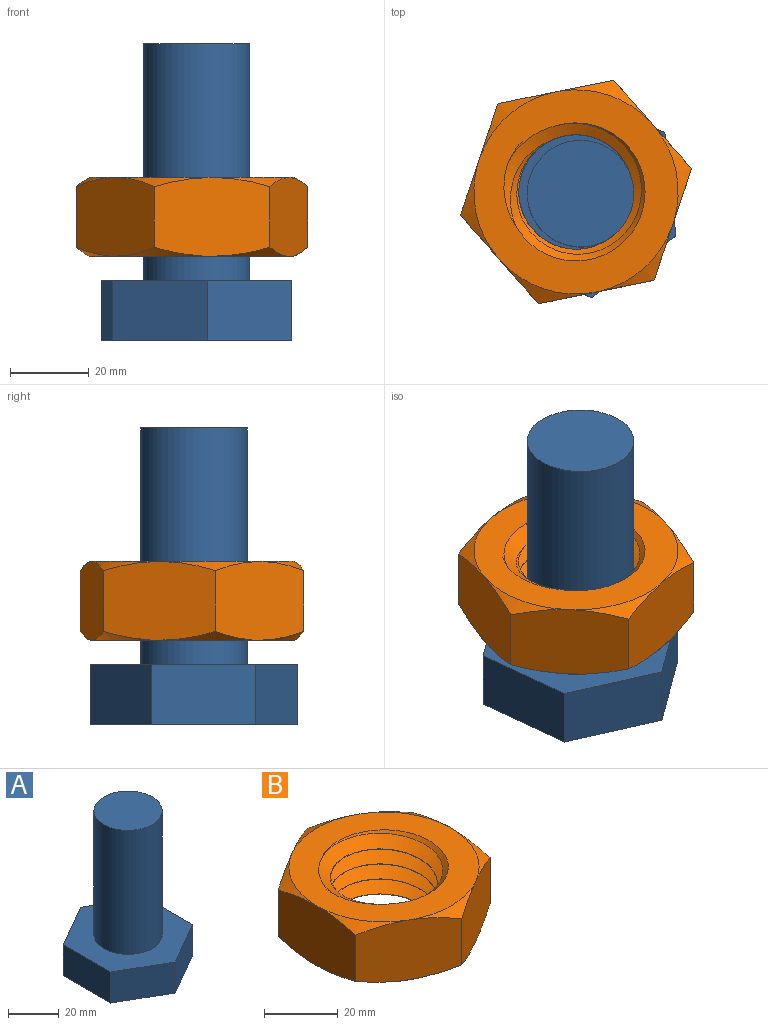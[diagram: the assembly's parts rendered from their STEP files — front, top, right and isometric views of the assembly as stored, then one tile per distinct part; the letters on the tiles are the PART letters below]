
ASSEMBLY  parts=2 mates=1
PART A: 10 faces, bbox 45.8x52.9x75 mm
  f0: cylinder r=13.5mm len=60mm, axis (0,0,-1), area 5089.4mm2, adj f1,f8
  f1: plane 27x27mm, normal (0,0,1), area 572.6mm2, adj f0
  f2: plane 22.91x15mm, normal (-0.5,0.87,0), area 396.7mm2, adj f3,f7,f8,f9
  f3: plane 26.45x15mm, normal (-1,0,0), area 396.7mm2, adj f2,f4,f8,f9
  f4: plane 22.91x15mm, normal (-0.5,-0.87,0), area 396.7mm2, adj f3,f5,f8,f9
  f5: plane 22.91x15mm, normal (0.5,-0.87,0), area 396.7mm2, adj f4,f6,f8,f9
  f6: plane 26.45x15mm, normal (1,0,0), area 396.7mm2, adj f5,f7,f8,f9
  f7: plane 22.91x15mm, normal (0.5,0.87,0), area 396.7mm2, adj f2,f6,f8,f9
  f8: plane 52.9x45.81mm, normal (0,0,1), area 1245.1mm2, adj f0,f2,f3,f4,f5,f6,f7
  f9: plane 52.9x45.81mm, normal (0,0,-1), area 1817.6mm2, adj f2,f3,f4,f5,f6,f7
PART B: 19 faces, bbox 60x60.1x26 mm
  f0: plane 25.86x20.01mm, normal (-0.5,0.87,0), area 550.1mm2, adj f1,f5,f8,f9,f10,f15
  f1: plane 29.88x20.01mm, normal (-1,0,0), area 550.1mm2, adj f0,f2,f8,f9,f14,f15
  f2: plane 25.89x20.01mm, normal (-0.5,-0.87,0), area 550.1mm2, adj f1,f3,f8,f9,f13,f14
  f3: plane 25.86x20.01mm, normal (0.5,-0.87,0), area 550.1mm2, adj f2,f4,f8,f9,f12,f13
  f4: plane 29.88x20.01mm, normal (1,0,0), area 550.1mm2, adj f3,f5,f8,f9,f11,f12
  f5: plane 25.89x20.01mm, normal (0.5,0.87,0), area 550.1mm2, adj f0,f4,f8,f9,f10,f11
  f6: plane 51.71x51.71mm, normal (0,0,-1), area 1231.2mm2, adj f7,f9,f17,f18
  f7: cylinder r=14.5mm len=29mm, axis (0,0,-1), area 30.2mm2, adj f6,f16,f17,f18
  f8: plane 52.07x52.04mm, normal (0,0,1), area 1121.7mm2, adj f0,f1,f2,f3,f4,f5,f10,f11
  f9: cone r=39.73mm half-angle=60.2deg, axis (0,0,1), area 251.3mm2, adj f0,f1,f2,f3,f4,f5,f6
  f10: cone r=39.74mm half-angle=60deg, axis (0,0,-1), area 41.1mm2, adj f0,f5,f8
  f11: cone r=39.74mm half-angle=60deg, axis (0,0,-1), area 41.1mm2, adj f4,f5,f8
  f12: cone r=39.74mm half-angle=60deg, axis (0,0,-1), area 41.1mm2, adj f3,f4,f8
  f13: cone r=39.74mm half-angle=60deg, axis (0,0,-1), area 41.1mm2, adj f2,f3,f8
  f14: cone r=39.74mm half-angle=60deg, axis (0,0,-1), area 41.1mm2, adj f1,f2,f8
  f15: cone r=39.74mm half-angle=60deg, axis (0,0,-1), area 41.1mm2, adj f0,f1,f8
  f16: cone r=14.5mm half-angle=45deg, axis (0,0,1), area 161mm2, adj f7,f8,f17,f18
  f17: bspline ~43.29x37.49mm, area 1948.6mm2, adj f6,f7,f8,f16,f18
  f18: bspline ~43.29x37.49mm, area 1944.4mm2, adj f6,f7,f8,f16,f17
PLACE A rot(axis=(0,0,1),66.1deg) t=(-52.58,-20.08,-26.68)mm fixed
PLACE B rot(axis=(0,0,-1),18.6deg) t=(-53.72,-19.62,-5.51)mm
MATE cylindrical B.f6 <-> A.f0  axis (0,0,-1) through (-52.58,-20.08,-5.51)mm
